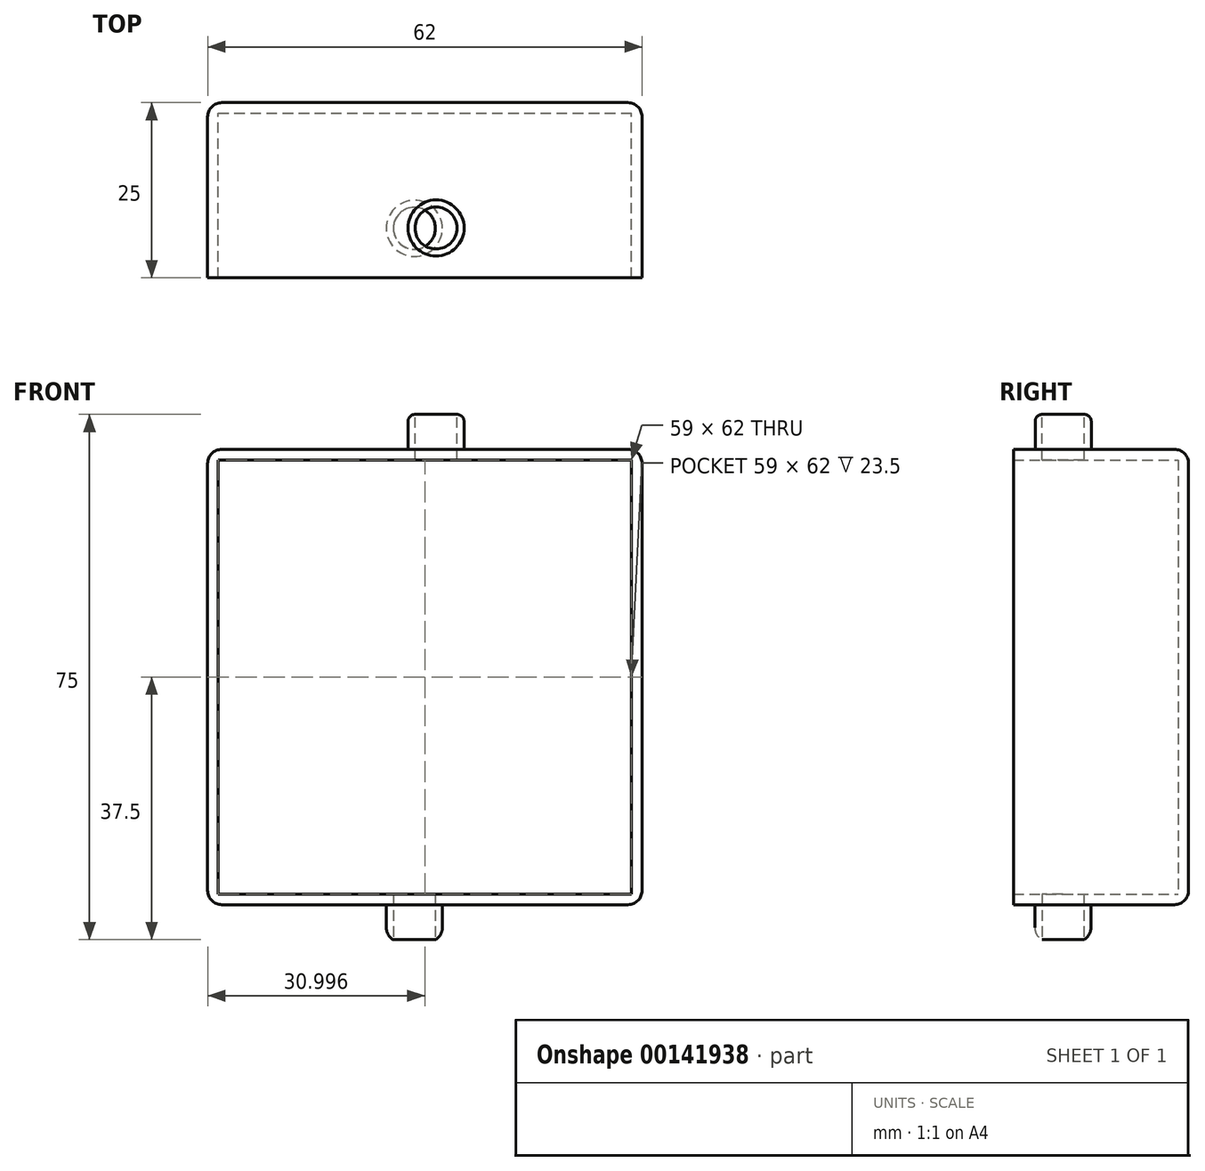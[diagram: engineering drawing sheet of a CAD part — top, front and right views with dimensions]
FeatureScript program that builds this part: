
annotation { "Feature Type Name" : "Feature", "Feature Type Description" : "" }
export const myFeature = defineFeature(function(context is Context, id is Id, definition is map)
    precondition{}
    {
        {
            var Q0;
            Q0=qCreatedBy(makeId("Front.planeOp"),FACE);
            var sketch = newSketch(context, id + "F0", { "sketchPlane" : qUnion([Q0])});
            skLineSegment(sketch, "E0.bottom", {"start": v(-57.4, 63.4) * mm, "end": v(1.6, 63.4) * mm});
            skLineSegment(sketch, "E0.top", {"start": v(-57.4, 1.4) * mm, "end": v(1.6, 1.4) * mm});
            skLineSegment(sketch, "E0.left", {"start": v(-57.4, 63.4) * mm, "end": v(-57.4, 1.4) * mm});
            skLineSegment(sketch, "E0.right", {"start": v(1.6, 63.4) * mm, "end": v(1.6, 1.4) * mm});
            skLineSegment(sketch, "E1.bottom", {"start": v(-58.9, 64.9) * mm, "end": v(3.1, 64.9) * mm});
            skLineSegment(sketch, "E1.top", {"start": v(-58.9, -0.1) * mm, "end": v(3.1, -0.1) * mm});
            skLineSegment(sketch, "E1.left", {"start": v(-58.9, 64.9) * mm, "end": v(-58.9, -0.1) * mm});
            skLineSegment(sketch, "E1.right", {"start": v(3.1, 64.9) * mm, "end": v(3.1, -0.1) * mm});
            skSolve(sketch);
        }
        {
            var Q0;
            Q0=makeQuery(id+"F0.imprint","IMPRINT",FACE,{"disambiguationData":[TD([[makeQuery(id+"F0.imprint","IMPRINT",EDGE,{"derivedFrom":sQuery(id+"F0.wireOp",EDGE,"E0.bottom")}),-1.0]])]});
            extrude(context, id + "F1", {"entities" : qUnion([Q0]), "depth" : 1.5 * mm});
        }
        {
            var Q0;
            Q0=makeQuery(id+"F0.imprint","IMPRINT",FACE,{"disambiguationData":[TD([[makeQuery(id+"F0.imprint","IMPRINT",EDGE,{"derivedFrom":sQuery(id+"F0.wireOp",EDGE,"E0.bottom")}),1.0]])]});
            extrude(context, id + "F2", {"entities" : qUnion([Q0]), "operationType" : NewBodyOperationType.ADD, "depth" : 25 * mm});
        }
        {
            var Q0;
            Q0=makeQuery(id+"F2.opExtrude","SWEPT_FACE",FACE,{"disambiguationData":[OSD([sQuery(id+"F0.wireOp",EDGE,"E1.top")])]});
            var sketch = newSketch(context, id + "F3", { "sketchPlane" : qUnion([Q0])});
            skCircle(sketch, "E2", {"center": v(-29.4, 17.94) * mm, "radius": 3 * mm});
            skCircle(sketch, "E3", {"center": v(-29.4, 17.94) * mm, "radius": 4 * mm});
            skSolve(sketch);
        }
        {
            var Q0;
            Q0=makeQuery(id+"F3.imprint","IMPRINT",FACE,{"disambiguationData":[TD([[makeQuery(id+"F3.imprint","IMPRINT",EDGE,{"derivedFrom":sQuery(id+"F3.wireOp",EDGE,"ImIwdinY-eUIE-Jf2U-P2t8-utrb5KvrqXSP")}),1.0]])]});
            var Q1;
            Q1=makeQuery(id+"F3.imprint","IMPRINT",FACE,{"disambiguationData":[TD([[makeQuery(id+"F3.imprint","IMPRINT",EDGE,{"derivedFrom":sQuery(id+"F3.wireOp",EDGE,"E2")}),1.0]])]});
            var Q2;
            Q2=makeQuery(id+"F3.imprint","IMPRINT",FACE,{"disambiguationData":[TD([[makeQuery(id+"F3.imprint","IMPRINT",EDGE,{"derivedFrom":sQuery(id+"F3.wireOp",EDGE,"TRb9hlzh-2jEI-ed3A-cgYW-J3lUckx4YSSx")}),1.0]])]});
            extrude(context, id + "F4", {"entities" : qUnion([Q0, Q1, Q2]), "operationType" : NewBodyOperationType.REMOVE, "oppositeDirection" : true, "depth" : 25 * mm});
        }
        {
            var Q0;
            Q0=makeQuery(id+"F3.imprint","IMPRINT",FACE,{"disambiguationData":[TD([[makeQuery(id+"F3.imprint","IMPRINT",EDGE,{"derivedFrom":sQuery(id+"F3.wireOp",EDGE,"zAfeBLLb-XMWE-ML26-6y2X-uzfi5LAJQmgL")}),1.0]])]});
            var Q1;
            Q1=makeQuery(id+"F3.imprint","IMPRINT",FACE,{"disambiguationData":[TD([[makeQuery(id+"F3.imprint","IMPRINT",EDGE,{"derivedFrom":sQuery(id+"F3.wireOp",EDGE,"TRb9hlzh-2jEI-ed3A-cgYW-J3lUckx4YSSx")}),-1.0]])]});
            var Q2;
            Q2=makeQuery(id+"F3.imprint","IMPRINT",FACE,{"disambiguationData":[TD([[makeQuery(id+"F3.imprint","IMPRINT",EDGE,{"derivedFrom":sQuery(id+"F3.wireOp",EDGE,"E2")}),-1.0]])]});
            extrude(context, id + "F5", {"entities" : qUnion([Q0, Q1, Q2]), "operationType" : NewBodyOperationType.ADD, "depth" : 5 * mm});
        }
        {
            var Q0;
            Q0=makeQuery(id+"F2.opExtrude","SWEPT_FACE",FACE,{"disambiguationData":[OSD([sQuery(id+"F0.wireOp",EDGE,"E1.bottom")])]});
            var sketch = newSketch(context, id + "F6", { "sketchPlane" : qUnion([Q0])});
            skCircle(sketch, "E4", {"center": v(-26.3, -17.89) * mm, "radius": 3 * mm});
            skCircle(sketch, "E5", {"center": v(-26.3, -17.89) * mm, "radius": 4 * mm});
            skSolve(sketch);
        }
        {
            var Q0;
            Q0=makeQuery(id+"F6.imprint","IMPRINT",FACE,{"disambiguationData":[TD([[makeQuery(id+"F6.imprint","IMPRINT",EDGE,{"derivedFrom":sQuery(id+"F6.wireOp",EDGE,"8905b46a-f214-4741-bd2d-deee052eeba0")}),1.0]])]});
            var Q1;
            Q1=makeQuery(id+"F6.imprint","IMPRINT",FACE,{"disambiguationData":[TD([[makeQuery(id+"F6.imprint","IMPRINT",EDGE,{"derivedFrom":sQuery(id+"F6.wireOp",EDGE,"E4")}),1.0]])]});
            var Q2;
            Q2=makeQuery(id+"F6.imprint","IMPRINT",FACE,{"disambiguationData":[TD([[makeQuery(id+"F6.imprint","IMPRINT",EDGE,{"derivedFrom":sQuery(id+"F6.wireOp",EDGE,"e02afdf0-ccc1-4bd0-b025-63cde9e4ef1c")}),1.0]])]});
            extrude(context, id + "F7", {"entities" : qUnion([Q0, Q1, Q2]), "operationType" : NewBodyOperationType.REMOVE, "oppositeDirection" : true, "depth" : 25 * mm});
        }
        {
            var Q0;
            Q0=makeQuery(id+"F6.imprint","IMPRINT",FACE,{"disambiguationData":[TD([[makeQuery(id+"F6.imprint","IMPRINT",EDGE,{"derivedFrom":sQuery(id+"F6.wireOp",EDGE,"db7be73c-c0de-4f7b-a1c7-3c91500f9900")}),1.0]])]});
            var Q1;
            Q1=makeQuery(id+"F6.imprint","IMPRINT",FACE,{"disambiguationData":[TD([[makeQuery(id+"F6.imprint","IMPRINT",EDGE,{"derivedFrom":sQuery(id+"F6.wireOp",EDGE,"E4")}),-1.0]])]});
            var Q2;
            Q2=makeQuery(id+"F6.imprint","IMPRINT",FACE,{"disambiguationData":[TD([[makeQuery(id+"F6.imprint","IMPRINT",EDGE,{"derivedFrom":sQuery(id+"F6.wireOp",EDGE,"e02afdf0-ccc1-4bd0-b025-63cde9e4ef1c")}),-1.0]])]});
            extrude(context, id + "F8", {"entities" : qUnion([Q0, Q1, Q2]), "operationType" : NewBodyOperationType.ADD, "depth" : 5 * mm});
        }
        {
            var Q0;
            Q0=makeQuery(id+"F2.opExtrude","CAP_EDGE",EDGE,{"disambiguationData":[OSD([sQuery(id+"F0.wireOp",EDGE,"E1.left")])],"isStart":true});
            var Q1;
            Q1=makeQuery(id+"F2.opExtrude","SWEPT_EDGE",EDGE,{"disambiguationData":[OSD([sQuery(id+"F0.wireOp",EDGE,"E1.top"),sQuery(id+"F0.wireOp",EDGE,"E1.left")])]});
            var Q2;
            Q2=makeQuery(id+"F2.opExtrude","SWEPT_EDGE",EDGE,{"disambiguationData":[OSD([sQuery(id+"F0.wireOp",EDGE,"E1.bottom"),sQuery(id+"F0.wireOp",EDGE,"E1.left")])]});
            var Q3;
            Q3=makeQuery(id+"F2.opExtrude","CAP_EDGE",EDGE,{"disambiguationData":[OSD([sQuery(id+"F0.wireOp",EDGE,"E1.top")])],"isStart":true});
            var Q4;
            Q4=makeQuery(id+"F2.opExtrude","CAP_EDGE",EDGE,{"disambiguationData":[OSD([sQuery(id+"F0.wireOp",EDGE,"E1.bottom")])],"isStart":true});
            var Q5;
            Q5=makeQuery(id+"F2.opExtrude","SWEPT_EDGE",EDGE,{"disambiguationData":[OSD([sQuery(id+"F0.wireOp",EDGE,"E1.bottom"),sQuery(id+"F0.wireOp",EDGE,"E1.right")])]});
            var Q6;
            Q6=makeQuery(id+"F2.opExtrude","CAP_EDGE",EDGE,{"disambiguationData":[OSD([sQuery(id+"F0.wireOp",EDGE,"E1.right")])],"isStart":true});
            var Q7;
            Q7=makeQuery(id+"F2.opExtrude","SWEPT_EDGE",EDGE,{"disambiguationData":[OSD([sQuery(id+"F0.wireOp",EDGE,"E1.top"),sQuery(id+"F0.wireOp",EDGE,"E1.right")])]});
            fillet(context, id + "F9", {"entities" : qUnion([Q0, Q1, Q2, Q3, Q4, Q5, Q6, Q7]), "radius" : 2 * mm, "tangentPropagation" : true, "allowEdgeOverflow" : false});
        }
        {
            var Q0;
            Q0=makeQuery(id+"F8.opExtrude","CAP_EDGE",EDGE,{"disambiguationData":[OSD([sQuery(id+"F6.wireOp",EDGE,"2e843606-c594-4e72-99ef-e6f6b912026b")])],"isStart":false});
            var Q1;
            Q1=makeQuery(id+"F8.opExtrude","CAP_EDGE",EDGE,{"disambiguationData":[OSD([sQuery(id+"F6.wireOp",EDGE,"E5")])],"isStart":false});
            var Q2;
            Q2=makeQuery(id+"F8.opExtrude","CAP_EDGE",EDGE,{"disambiguationData":[OSD([sQuery(id+"F6.wireOp",EDGE,"db7be73c-c0de-4f7b-a1c7-3c91500f9900")])],"isStart":false});
            fillet(context, id + "F10", {"entities" : qUnion([Q0, Q1, Q2]), "radius" : 1 * mm, "tangentPropagation" : true, "allowEdgeOverflow" : false});
        }
        {
            var Q0;
            Q0=makeQuery(id+"F5.opExtrude","CAP_EDGE",EDGE,{"disambiguationData":[OSD([sQuery(id+"F3.wireOp",EDGE,"zAfeBLLb-XMWE-ML26-6y2X-uzfi5LAJQmgL")])],"isStart":false});
            var Q1;
            Q1=makeQuery(id+"F5.opExtrude","CAP_EDGE",EDGE,{"disambiguationData":[OSD([sQuery(id+"F3.wireOp",EDGE,"E3")])],"isStart":false});
            var Q2;
            Q2=makeQuery(id+"F5.opExtrude","CAP_EDGE",EDGE,{"disambiguationData":[OSD([sQuery(id+"F3.wireOp",EDGE,"RaQPAUa7-unxy-unN2-nYZ3-VVTq4n9eoWD9")])],"isStart":false});
            fillet(context, id + "F11", {"entities" : qUnion([Q0, Q1, Q2]), "radius" : 2 * mm, "tangentPropagation" : true, "allowEdgeOverflow" : false});
        }
        {
            var Q0;
            Q0=makeQuery(id+"F1.opExtrude","SWEPT_BODY",BODY,{"disambiguationData":[OSD([sQuery(id+"F0.wireOp",EDGE,"E0.bottom"),sQuery(id+"F0.wireOp",EDGE,"E0.top"),sQuery(id+"F0.wireOp",EDGE,"E0.left"),sQuery(id+"F0.wireOp",EDGE,"E0.right")])]});
            transform(context, id + "F12", {"entities" : qUnion([Q0]), "transformType" : TransformType.TRANSLATION_3D, "dx" : 0 * mm, "dy" : 0 * mm, "dz" : 0 * mm, "makeCopy" : true});
        }
        {
            var Q0;
            Q0=makeQuery(id+"F12.opPattern","COPY",BODY,{"derivedFrom":makeQuery(id+"F1.opExtrude","SWEPT_BODY",BODY,{"disambiguationData":[OSD([sQuery(id+"F0.wireOp",EDGE,"E0.bottom"),sQuery(id+"F0.wireOp",EDGE,"E0.top"),sQuery(id+"F0.wireOp",EDGE,"E0.left"),sQuery(id+"F0.wireOp",EDGE,"E0.right")])]}),"instanceName":"1"});
            deleteBodies(context, id + "F13", {"entities" : qUnion([Q0])});
        }
        {
            var Q0;
            Q0=makeQuery(id+"F1.opExtrude","SWEPT_BODY",BODY,{"disambiguationData":[OSD([sQuery(id+"F0.wireOp",EDGE,"E0.bottom"),sQuery(id+"F0.wireOp",EDGE,"E0.top"),sQuery(id+"F0.wireOp",EDGE,"E0.left"),sQuery(id+"F0.wireOp",EDGE,"E0.right")])]});
            transform(context, id + "F14", {"entities" : qUnion([Q0]), "transformType" : TransformType.TRANSLATION_3D, "dx" : 0 * mm, "dy" : 0 * mm, "dz" : 0 * mm, "makeCopy" : true});
        }
    });
